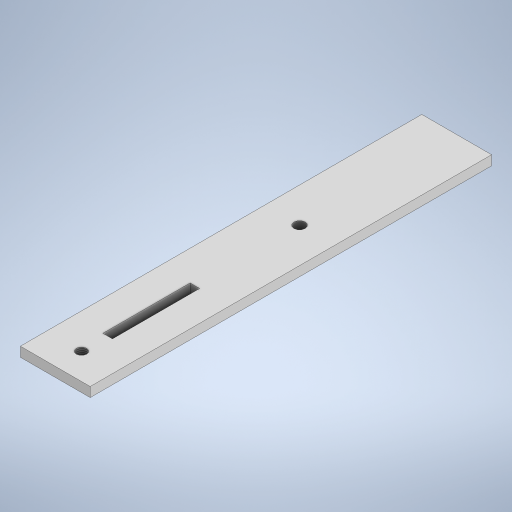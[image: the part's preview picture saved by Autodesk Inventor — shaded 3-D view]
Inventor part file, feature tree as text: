
AUTODESK INVENTOR PART (.ipt)
format: ipt  version: 2023 (Build 270158000, 158)  size: 249,344 bytes
history: native  units: mm
features: sketch x4, extrude x2, hole x2
ambient origin geometry x8: Origin, YZ Plane, XZ Plane, XY Plane, X Axis, Y Axis, Z Axis, Center Point
bodies: Solid1 (feature_tree)
feature tree (8):
  extrude  "Extrusion1"  Depth=40.0mm
  extrude  "Extrusion2"  Depth=30.0mm
  hole  "Hole1"  [1 undecoded]
  hole  "Hole2"  [1 undecoded]
  sketch  "Sketch1"  dims[d0=230.0mm d1=40.0mm]
  sketch  "Sketch2"  dims[d2=5.5mm d3=0.0mm d4=30.0mm]
  sketch  "Sketch3"  dims[d5=2.75mm d6=50.0mm]
  sketch  "Sketch4"  dims[d7=5.5mm d8=0.0mm d9=15.0mm d10=5.917468mm d11=14.0mm d12=4.0mm d13=2.0mm d14=90.0deg d15=19.1mm d16=20.594885mm d17=90.0mm d18=6.458734mm d19=14.0mm d20=4.0mm d21=2.0mm d22=90.0deg d23=19.1mm d24=20.594885mm]
note: 2 required parameter values undecoded (feature->parameter linkage not recoverable at this tier; creation-order binding heuristic only, values carry confidence <= 0.55)
